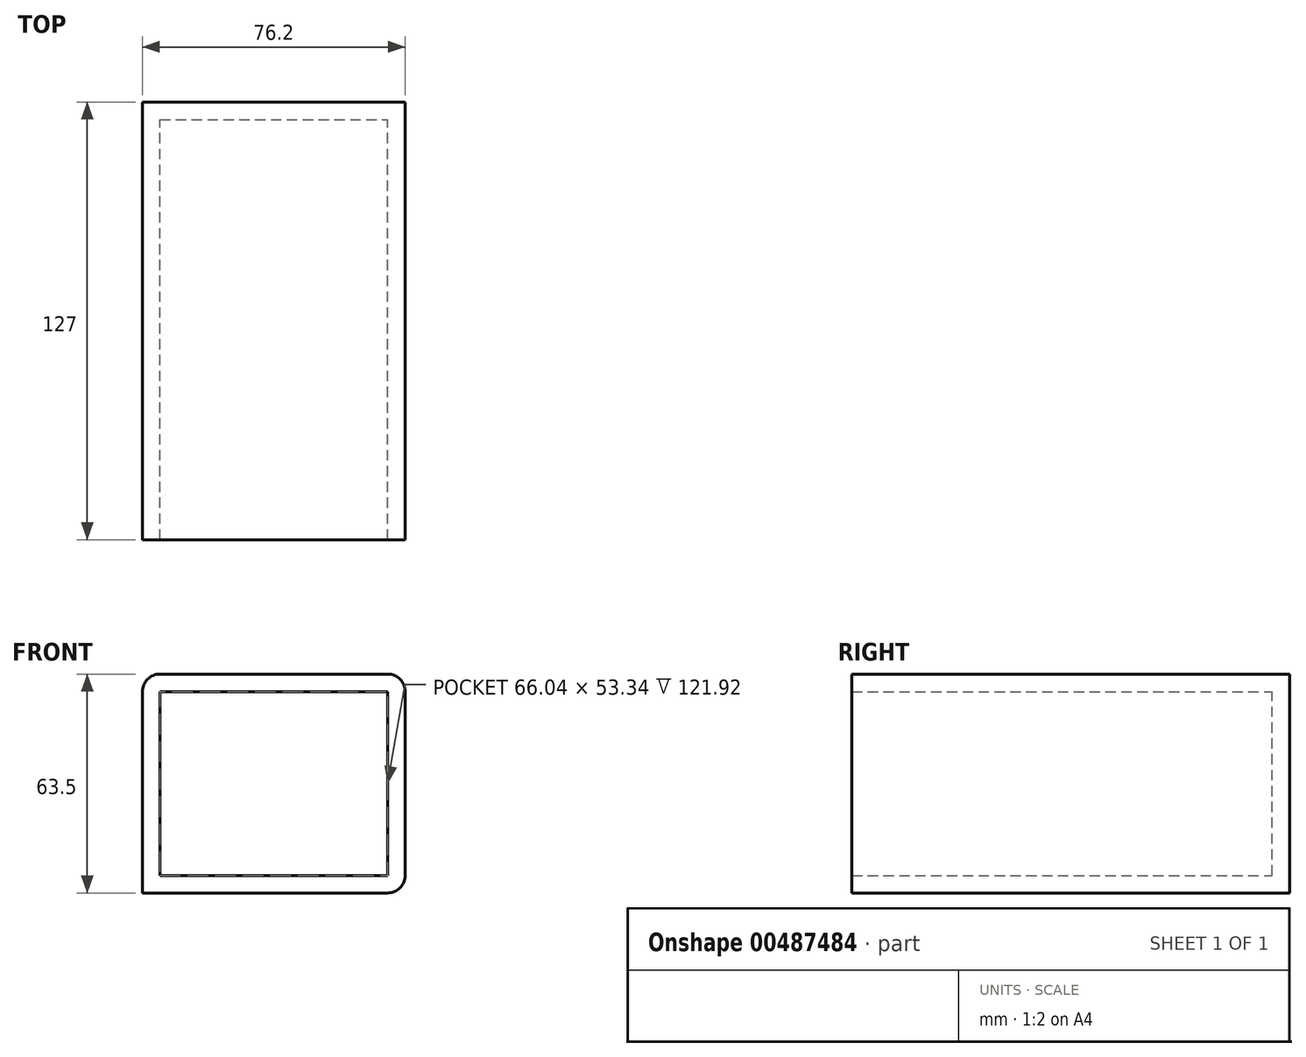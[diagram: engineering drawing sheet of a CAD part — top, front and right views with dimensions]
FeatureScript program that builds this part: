
annotation { "Feature Type Name" : "Feature", "Feature Type Description" : "" }
export const myFeature = defineFeature(function(context is Context, id is Id, definition is map)
    precondition{}
    {
        {
            var Q0;
            Q0=qCreatedBy(makeId("Front.planeOp"),FACE);
            var sketch = newSketch(context, id + "F0", { "sketchPlane" : qUnion([Q0])});
            skLineSegment(sketch, "E0.bottom", {"start": v(0, -2.82) * mm, "end": v(76.2, -2.82) * mm});
            skLineSegment(sketch, "E0.top", {"start": v(0, 60.68) * mm, "end": v(76.2, 60.68) * mm});
            skLineSegment(sketch, "E0.left", {"start": v(0, -2.82) * mm, "end": v(0, 60.68) * mm});
            skLineSegment(sketch, "E0.right", {"start": v(76.2, -2.82) * mm, "end": v(76.2, 60.68) * mm});
            skSolve(sketch);
        }
        {
            var Q0;
            Q0=makeQuery(id+"F0.imprint","IMPRINT",FACE,{"disambiguationData":[TD([[makeQuery(id+"F0.imprint","IMPRINT",EDGE,{"derivedFrom":sQuery(id+"F0.wireOp",EDGE,"E0.bottom")}),1.0]])]});
            extrude(context, id + "F1", {"entities" : qUnion([Q0]), "depth" : 127 * mm});
        }
        {
            var Q0;
            Q0=makeQuery(id+"F1.opExtrude","CAP_FACE",FACE,{"disambiguationData":[OSD([sQuery(id+"F0.wireOp",EDGE,"E0.bottom"),sQuery(id+"F0.wireOp",EDGE,"E0.top"),sQuery(id+"F0.wireOp",EDGE,"E0.left"),sQuery(id+"F0.wireOp",EDGE,"E0.right")])],"isStart":false});
            shell(context, id + "F2", {"entities" : qUnion([Q0]), "thickness" : 5.08 * mm});
        }
        {
            var Q0;
            Q0=makeQuery(id+"F1.opExtrude","SWEPT_EDGE",EDGE,{"disambiguationData":[OSD([sQuery(id+"F0.wireOp",EDGE,"E0.top"),sQuery(id+"F0.wireOp",EDGE,"E0.right")])]});
            var Q1;
            Q1=makeQuery(id+"F1.opExtrude","SWEPT_EDGE",EDGE,{"disambiguationData":[OSD([sQuery(id+"F0.wireOp",EDGE,"E0.top"),sQuery(id+"F0.wireOp",EDGE,"E0.left")])]});
            var Q2;
            Q2=makeQuery(id+"F1.opExtrude","SWEPT_EDGE",EDGE,{"disambiguationData":[OSD([sQuery(id+"F0.wireOp",EDGE,"E0.bottom"),sQuery(id+"F0.wireOp",EDGE,"E0.right")])]});
            fillet(context, id + "F3", {"entities" : qUnion([Q0, Q1, Q2]), "radius" : 5.08 * mm, "tangentPropagation" : true, "allowEdgeOverflow" : false});
        }
    });
